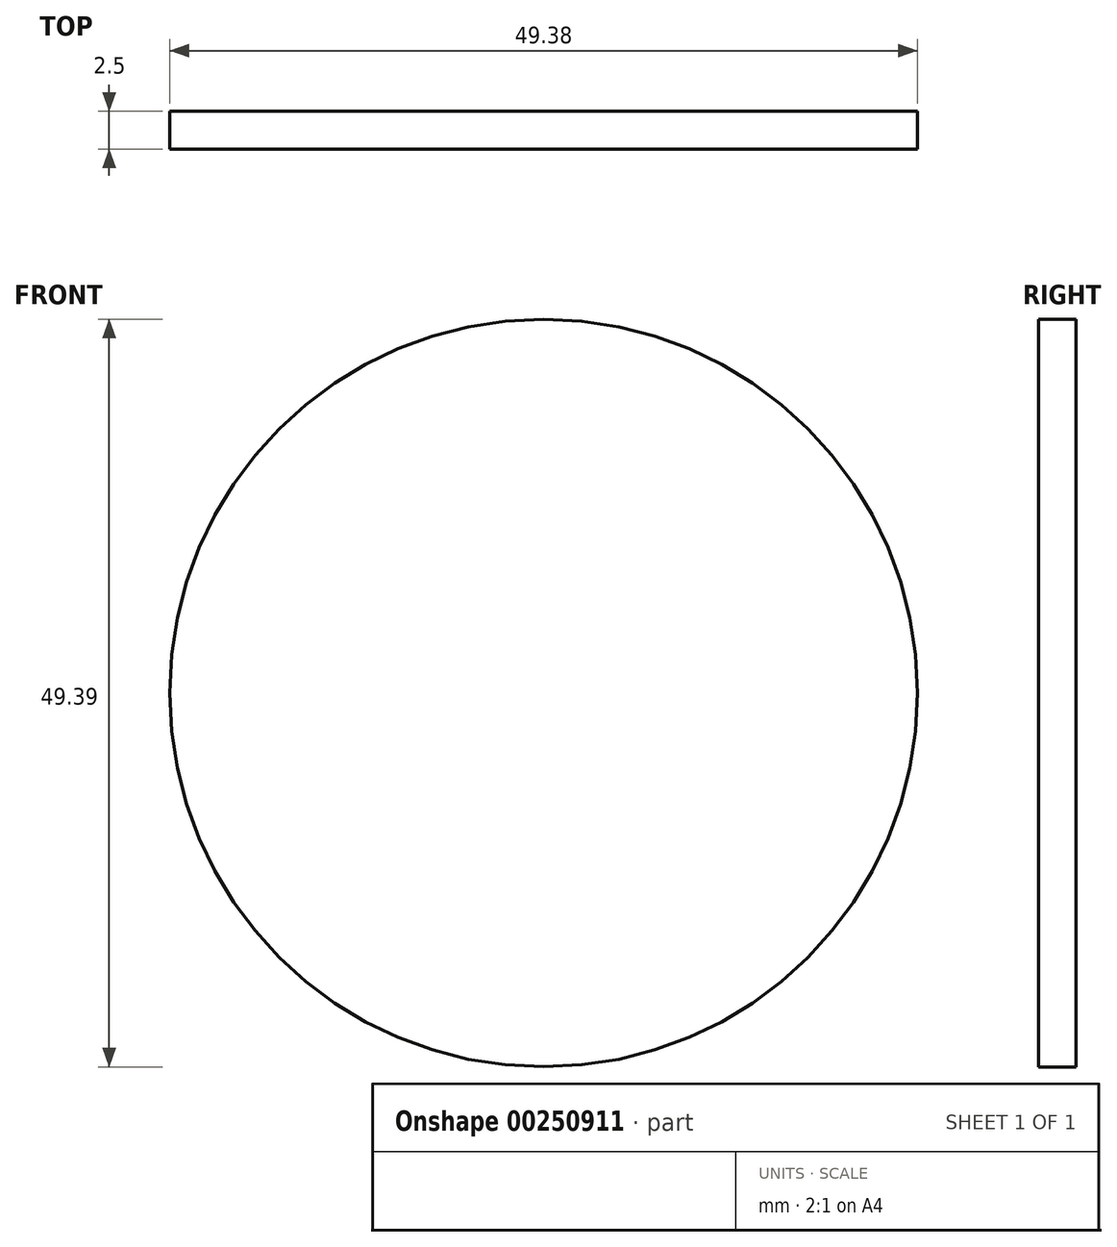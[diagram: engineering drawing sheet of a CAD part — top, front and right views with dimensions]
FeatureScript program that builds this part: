
annotation { "Feature Type Name" : "Feature", "Feature Type Description" : "" }
export const myFeature = defineFeature(function(context is Context, id is Id, definition is map)
    precondition{}
    {
        {
            var Q0;
            Q0=qCreatedBy(makeId("Front.planeOp"),FACE);
            var sketch = newSketch(context, id + "F0", { "sketchPlane" : qUnion([Q0])});
            skLineSegment(sketch, "E0.bottom", {"start": v(34, 70) * mm, "end": v(-34, 70) * mm});
            skLineSegment(sketch, "E0.top", {"start": v(34, -70) * mm, "end": v(-34, -70) * mm});
            skLineSegment(sketch, "E0.left", {"start": v(34, 70) * mm, "end": v(34, -70) * mm});
            skLineSegment(sketch, "E0.right", {"start": v(-34, 70) * mm, "end": v(-34, -70) * mm});
            skPoint(sketch, "E0.middle", {"position": v(0, 0) * mm});
            skSolve(sketch);
        }
        {
            var Q0;
            Q0=makeQuery(id+"F0.imprint","IMPRINT",FACE,{"disambiguationData":[TD([[makeQuery(id+"F0.imprint","IMPRINT",EDGE,{"derivedFrom":sQuery(id+"F0.wireOp",EDGE,"E0.bottom")}),1.0]])]});
            extrude(context, id + "F1", {"entities" : qUnion([Q0]), "endBound" : BoundingType.SYMMETRIC, "depth" : 25 * mm});
        }
        {
            var Q0;
            Q0=makeQuery(id+"F1.opExtrude","CAP_FACE",FACE,{"disambiguationData":[OSD([sQuery(id+"F0.wireOp",EDGE,"E0.bottom"),sQuery(id+"F0.wireOp",EDGE,"E0.top"),sQuery(id+"F0.wireOp",EDGE,"E0.left"),sQuery(id+"F0.wireOp",EDGE,"E0.right")])],"isStart":true});
            shell(context, id + "F2", {"entities" : qUnion([Q0]), "thickness" : 2.5 * mm});
        }
        {
            var Q0;
            Q0=makeQuery(id+"F1.opExtrude","CAP_FACE",FACE,{"disambiguationData":[OSD([sQuery(id+"F0.wireOp",EDGE,"E0.bottom"),sQuery(id+"F0.wireOp",EDGE,"E0.top"),sQuery(id+"F0.wireOp",EDGE,"E0.left"),sQuery(id+"F0.wireOp",EDGE,"E0.right")])],"isStart":false});
            var sketch = newSketch(context, id + "F3", { "sketchPlane" : qUnion([Q0])});
            skCircle(sketch, "E1", {"center": v(0, 42.17) * mm, "radius": 24.7 * mm});
            skCircle(sketch, "E2.MirrorC", {"center": v(0, -42.17) * mm, "radius": 24.7 * mm});
            skLineSegment(sketch, "E3", {"start": v(-34, 15.5) * mm, "end": v(-12.2, 0) * mm});
            skLineSegment(sketch, "E4.MirrorCS", {"start": v(-34, -15.5) * mm, "end": v(-12.2, 0) * mm});
            skSolve(sketch);
        }
        {
            var Q0;
            Q0=makeQuery(id+"F3.imprint","IMPRINT",FACE,{"disambiguationData":[TD([[makeQuery(id+"F3.imprint","IMPRINT",EDGE,{"derivedFrom":sQuery(id+"F3.wireOp",EDGE,"E1")}),1.0]])]});
            var Q1;
            Q1=makeQuery(id+"F3.imprint","IMPRINT",FACE,{"disambiguationData":[TD([[makeQuery(id+"F3.imprint","IMPRINT",EDGE,{"derivedFrom":sQuery(id+"F3.wireOp",EDGE,"E2.MirrorC")}),-1.0]])]});
            var Q2;
            {var subQ0=sQuery(id+"F3.wireOp",EDGE,"E3");Q2=makeQuery(id+"F3.imprint","IMPRINT",FACE,{"disambiguationData":[TD([[makeQuery(id+"F3.imprint","IMPRINT",EDGE,{"derivedFrom":subQ0}),-1.0]])]});}
            extrude(context, id + "F4", {"entities" : qUnion([Q0, Q1, Q2]), "operationType" : NewBodyOperationType.REMOVE, "endBound" : BoundingType.SYMMETRIC, "depth" : 300 * mm});
        }
        {
            var Q0;
            Q0=makeQuery(id+"F1.opExtrude","SWEPT_FACE",FACE,{"disambiguationData":[OSD([sQuery(id+"F0.wireOp",EDGE,"E0.left")])]});
            var sketch = newSketch(context, id + "F5", { "sketchPlane" : qUnion([Q0])});
            skLineSegment(sketch, "E5.bottom", {"start": v(3.73, -58.1) * mm, "end": v(-3.73, -58.1) * mm});
            skLineSegment(sketch, "E5.top", {"start": v(3.73, -27.11) * mm, "end": v(-3.73, -27.11) * mm});
            skLineSegment(sketch, "E5.left", {"start": v(3.73, -58.1) * mm, "end": v(3.73, -27.11) * mm});
            skLineSegment(sketch, "E5.right", {"start": v(-3.73, -58.1) * mm, "end": v(-3.73, -27.11) * mm});
            skPoint(sketch, "E5.middle", {"position": v(0, -42.6) * mm});
            skLineSegment(sketch, "E6.MirrorCS", {"start": v(3.73, 27.11) * mm, "end": v(-3.73, 27.11) * mm});
            skLineSegment(sketch, "E7.MirrorCS", {"start": v(3.73, 58.1) * mm, "end": v(3.73, 27.11) * mm});
            skLineSegment(sketch, "E8.MirrorCS", {"start": v(-3.73, 58.1) * mm, "end": v(-3.73, 27.11) * mm});
            skLineSegment(sketch, "E9.MirrorCS", {"start": v(3.73, 58.1) * mm, "end": v(-3.73, 58.1) * mm});
            skSolve(sketch);
        }
        {
            var Q0;
            Q0=makeQuery(id+"F1.opExtrude","SWEPT_FACE",FACE,{"disambiguationData":[OSD([sQuery(id+"F0.wireOp",EDGE,"E0.bottom")])]});
            var sketch = newSketch(context, id + "F6", { "sketchPlane" : qUnion([Q0])});
            skSolve(sketch);
        }
    });
